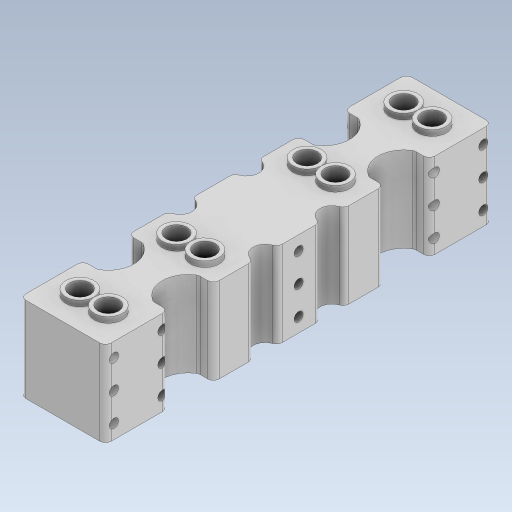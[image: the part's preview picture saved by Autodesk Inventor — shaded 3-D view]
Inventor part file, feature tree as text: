
AUTODESK INVENTOR PART (.ipt)
format: ipt  version: 2023.5 (Build 275446000, 446)  size: 355,840 bytes
history: native  units: mm
features: extrude x3, sketch x2, plane x1
ambient origin geometry x8: Origin, YZ Plane, XZ Plane, XY Plane, X Axis, Y Axis, Z Axis, Center Point
bodies: Solid1 (feature_tree)
feature tree (6):
  sketch  "Sketch1"  dims[d0=15.0mm d1=7.5mm]
  extrude  "Extrusion1"  Depth=7.5mm
  extrude  "Extrusion2"  Depth=10.0mm
  plane  "Work Plane1"
  extrude  "Extrusion3"  Depth=10.0mm
  sketch  "Sketch2"  dims[d2=7.3mm d3=23.0mm d4=10.0mm d6=7.3mm d7=10.0mm d8=34.0mm d9=4.0mm d10=4.0mm d11=2.0mm d12=2.0mm d13=30.0mm d14=0.0mm d15=32.0mm d16=0.0mm d17=3.2mm d18=3.2mm d19=5.0mm d20=3.2mm d21=3.2mm d22=3.2mm d23=3.2mm d24=32.0mm d25=0.0mm d26=3.2mm d27=3.2mm d28=3.2mm d29=3.2mm d30=3.2mm d31=3.2mm d32=3.2mm d33=3.2mm d34=3.2mm d35=2.0mm d36=2.0mm d37=2.0mm]
